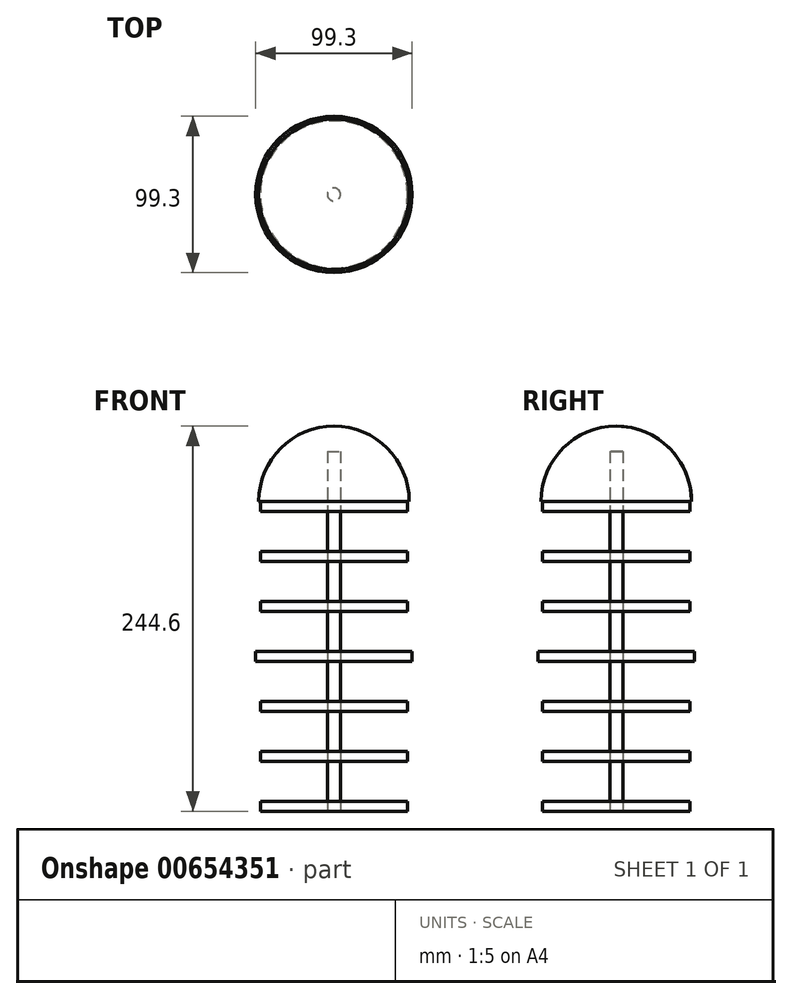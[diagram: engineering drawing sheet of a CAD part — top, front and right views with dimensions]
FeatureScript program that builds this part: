
annotation { "Feature Type Name" : "Feature", "Feature Type Description" : "" }
export const myFeature = defineFeature(function(context is Context, id is Id, definition is map)
    precondition{}
    {
        {
            var Q0;
            Q0=qCreatedBy(makeId("Top.planeOp"),FACE);
            var sketch = newSketch(context, id + "F0", { "sketchPlane" : qUnion([Q0])});
            skCircle(sketch, "E0", {"center": v(0, 0) * mm, "radius": 46.74 * mm});
            skSolve(sketch);
        }
        {
            var Q0;
            Q0=makeQuery(id+"F0.imprint","IMPRINT",FACE,{"disambiguationData":[TD([[makeQuery(id+"F0.imprint","IMPRINT",EDGE,{"derivedFrom":sQuery(id+"F0.wireOp",EDGE,"E0")}),1.0]])]});
            extrude(context, id + "F1", {"entities" : qUnion([Q0]), "depth" : 6.35 * mm, "offsetDistance" : 25.4 * mm});
        }
        {
            var Q0;
            Q0=makeQuery(id+"F1.opExtrude","CAP_FACE",FACE,{"disambiguationData":[OSD([sQuery(id+"F0.wireOp",EDGE,"E0")])],"isStart":false});
            cPlane(context, id + "F2", {"entities" : qUnion([Q0]), "cplaneType" : CPlaneType.OFFSET, "offset" : 25.4 * mm, "width" : 152.4 * mm, "height" : 152.4 * mm});
        }
        {
            var Q0;
            Q0=qCreatedBy(id+"F2.planeOp",FACE);
            var sketch = newSketch(context, id + "F3", { "sketchPlane" : qUnion([Q0])});
            skCircle(sketch, "E1", {"center": v(0, 0) * mm, "radius": 46.74 * mm});
            skSolve(sketch);
        }
        {
            var Q0;
            Q0 = qSketchRegion(id + "F3", true);
            extrude(context, id + "F4", {"entities" : qUnion([Q0]), "depth" : 6.35 * mm, "offsetDistance" : 25.4 * mm});
        }
        {
            var Q0;
            Q0=makeQuery(id+"F4.opExtrude","CAP_FACE",FACE,{"disambiguationData":[OSD([sQuery(id+"F3.wireOp",EDGE,"E1")])],"isStart":false});
            cPlane(context, id + "F5", {"entities" : qUnion([Q0]), "cplaneType" : CPlaneType.OFFSET, "offset" : 25.4 * mm, "width" : 152.4 * mm, "height" : 152.4 * mm});
        }
        {
            var Q0;
            Q0=qCreatedBy(id+"F5.planeOp",FACE);
            var sketch = newSketch(context, id + "F6", { "sketchPlane" : qUnion([Q0])});
            skCircle(sketch, "E2", {"center": v(0, 0) * mm, "radius": 46.74 * mm});
            skSolve(sketch);
        }
        {
            var Q0;
            Q0=makeQuery(id+"F6.imprint","IMPRINT",FACE,{"disambiguationData":[TD([[makeQuery(id+"F6.imprint","IMPRINT",EDGE,{"derivedFrom":sQuery(id+"F6.wireOp",EDGE,"E2")}),1.0]])]});
            extrude(context, id + "F7", {"entities" : qUnion([Q0]), "depth" : 6.35 * mm, "offsetDistance" : 25.4 * mm});
        }
        {
            var Q0;
            Q0=makeQuery(id+"F7.opExtrude","CAP_FACE",FACE,{"disambiguationData":[OSD([sQuery(id+"F6.wireOp",EDGE,"E2")])],"isStart":false});
            cPlane(context, id + "F8", {"entities" : qUnion([Q0]), "cplaneType" : CPlaneType.OFFSET, "offset" : 25.4 * mm, "width" : 152.4 * mm, "height" : 152.4 * mm});
        }
        {
            var Q0;
            Q0=qCreatedBy(id+"F8.planeOp",FACE);
            var sketch = newSketch(context, id + "F9", { "sketchPlane" : qUnion([Q0])});
            skCircle(sketch, "E3", {"center": v(0, 0) * mm, "radius": 49.65 * mm});
            skSolve(sketch);
        }
        {
            var Q0;
            Q0=makeQuery(id+"F9.imprint","IMPRINT",FACE,{"disambiguationData":[TD([[makeQuery(id+"F9.imprint","IMPRINT",EDGE,{"derivedFrom":sQuery(id+"F9.wireOp",EDGE,"E3")}),1.0]])]});
            extrude(context, id + "F10", {"entities" : qUnion([Q0]), "depth" : 6.35 * mm, "offsetDistance" : 25.4 * mm});
        }
        {
            var Q0;
            Q0=makeQuery(id+"F10.opExtrude","CAP_FACE",FACE,{"disambiguationData":[OSD([sQuery(id+"F9.wireOp",EDGE,"E3")])],"isStart":false});
            cPlane(context, id + "F11", {"entities" : qUnion([Q0]), "cplaneType" : CPlaneType.OFFSET, "offset" : 25.4 * mm, "width" : 152.4 * mm, "height" : 152.4 * mm});
        }
        {
            var Q0;
            Q0=qCreatedBy(id+"F11.planeOp",FACE);
            var sketch = newSketch(context, id + "F12", { "sketchPlane" : qUnion([Q0])});
            skCircle(sketch, "E4", {"center": v(0, 0) * mm, "radius": 46.74 * mm});
            skSolve(sketch);
        }
        {
            var Q0;
            Q0=makeQuery(id+"F12.imprint","IMPRINT",FACE,{"disambiguationData":[TD([[makeQuery(id+"F12.imprint","IMPRINT",EDGE,{"derivedFrom":sQuery(id+"F12.wireOp",EDGE,"E4")}),1.0]])]});
            extrude(context, id + "F13", {"entities" : qUnion([Q0]), "depth" : 6.35 * mm, "offsetDistance" : 25.4 * mm});
        }
        {
            var Q0;
            Q0=makeQuery(id+"F13.opExtrude","CAP_FACE",FACE,{"disambiguationData":[OSD([sQuery(id+"F12.wireOp",EDGE,"E4")])],"isStart":false});
            cPlane(context, id + "F14", {"entities" : qUnion([Q0]), "cplaneType" : CPlaneType.OFFSET, "offset" : 25.4 * mm, "width" : 152.4 * mm, "height" : 152.4 * mm});
        }
        {
            var Q0;
            Q0=qCreatedBy(id+"F14.planeOp",FACE);
            var sketch = newSketch(context, id + "F15", { "sketchPlane" : qUnion([Q0])});
            skCircle(sketch, "E5", {"center": v(0, 0) * mm, "radius": 46.74 * mm});
            skSolve(sketch);
        }
        {
            var Q0;
            Q0=makeQuery(id+"F15.imprint","IMPRINT",FACE,{"disambiguationData":[TD([[makeQuery(id+"F15.imprint","IMPRINT",EDGE,{"derivedFrom":sQuery(id+"F15.wireOp",EDGE,"E5")}),1.0]])]});
            extrude(context, id + "F16", {"entities" : qUnion([Q0]), "depth" : 6.35 * mm, "offsetDistance" : 25.4 * mm});
        }
        {
            var Q0;
            Q0=makeQuery(id+"F16.opExtrude","CAP_FACE",FACE,{"disambiguationData":[OSD([sQuery(id+"F15.wireOp",EDGE,"E5")])],"isStart":false});
            cPlane(context, id + "F17", {"entities" : qUnion([Q0]), "cplaneType" : CPlaneType.OFFSET, "offset" : 25.4 * mm, "width" : 152.4 * mm, "height" : 152.4 * mm});
        }
        {
            var Q0;
            Q0=qCreatedBy(id+"F17.planeOp",FACE);
            var sketch = newSketch(context, id + "F18", { "sketchPlane" : qUnion([Q0])});
            skCircle(sketch, "E6", {"center": v(0, 0) * mm, "radius": 46.74 * mm});
            skSolve(sketch);
        }
        {
            var Q0;
            Q0=makeQuery(id+"F18.imprint","IMPRINT",FACE,{"disambiguationData":[TD([[makeQuery(id+"F18.imprint","IMPRINT",EDGE,{"derivedFrom":sQuery(id+"F18.wireOp",EDGE,"E6")}),1.0]])]});
            extrude(context, id + "F19", {"entities" : qUnion([Q0]), "depth" : 6.35 * mm, "offsetDistance" : 25.4 * mm});
        }
        {
            var Q0;
            Q0=qCreatedBy(makeId("Right.planeOp"),FACE);
            var sketch = newSketch(context, id + "F20", { "sketchPlane" : qUnion([Q0])});
            skArc(sketch, "E7", {"start": v(0, 244.6) * mm, "mid": v(-33.77, 230.62) * mm, "end": v(-47.75, 196.85) * mm});
            skLineSegment(sketch, "E8", {"start": v(-47.75, 196.85) * mm, "end": v(0, 196.85) * mm});
            skLineSegment(sketch, "E9", {"start": v(0, 244.6) * mm, "end": v(0, 196.85) * mm});
            skSolve(sketch);
        }
        {
            var Q0;
            Q0=makeQuery(id+"F20.imprint","IMPRINT",FACE,{"disambiguationData":[TD([[makeQuery(id+"F20.imprint","IMPRINT",EDGE,{"derivedFrom":sQuery(id+"F20.wireOp",EDGE,"E7")}),1.0]])]});
            var Q1;
            Q1=sQuery(id+"F20.wireOp",EDGE,"E9");
            revolve(context, id + "F21", {"operationType" : NewBodyOperationType.ADD, "entities" : qUnion([Q0]), "axis" : qUnion([Q1]), "revolveType" : RevolveType.FULL});
        }
        {
            var Q0;
            Q0=makeQuery(id+"F1.opExtrude","CAP_FACE",FACE,{"disambiguationData":[OSD([sQuery(id+"F0.wireOp",EDGE,"E0")])],"isStart":true});
            var sketch = newSketch(context, id + "F22", { "sketchPlane" : qUnion([Q0])});
            skCircle(sketch, "E10", {"center": v(0, 0) * mm, "radius": 4.15 * mm});
            skSolve(sketch);
        }
        {
            var Q0;
            Q0=makeQuery(id+"F22.imprint","IMPRINT",FACE,{"disambiguationData":[TD([[makeQuery(id+"F22.imprint","IMPRINT",EDGE,{"derivedFrom":sQuery(id+"F22.wireOp",EDGE,"E10")}),1.0]])]});
            extrude(context, id + "F23", {"entities" : qUnion([Q0]), "oppositeDirection" : true, "depth" : 228.6 * mm, "offsetDistance" : 25.4 * mm});
        }
    });
